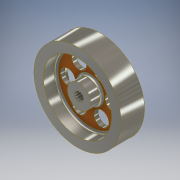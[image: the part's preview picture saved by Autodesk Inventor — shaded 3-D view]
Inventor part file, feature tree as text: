
AUTODESK INVENTOR PART (.ipt)
format: ipt  version: 2017 (Build 210142000, 142)  size: 212,480 bytes
history: native  units: mm
features: extrude x7, sketch x7, fillet x3, plane x2, chamfer x1
ambient origin geometry x8: Origin, YZ Plane, XZ Plane, XY Plane, X Axis, Y Axis, Z Axis, Center Point
bodies: Solid1 (feature_tree)
feature tree (20):
  extrude  "Extrusion1"  Depth=22.0mm TaperAngle=0.0deg
  extrude  "Extrusion2"  Depth=6.0mm TaperAngle=0.0deg
  extrude  "Extrusion3"  Depth=12.0mm TaperAngle=0.0deg
  plane  "Work Plane1"
  extrude  "Extrusion4"  Depth=22.0mm
  extrude  "Extrusion5"  Depth=22.0mm
  plane  "Work Plane2"
  extrude  "Extrusion6"  [1 undecoded]
  extrude  "Extrusion7"  Depth=10.0mm TaperAngle=0.0deg
  fillet  "Fillet1"  Radius=14.0mm
  fillet  "Fillet2"  Radius=60.0mm
  fillet  "Fillet3"  [1 undecoded]
  chamfer  "Chamfer1"  Distance=2.0mm
  sketch  "Sketch1"  dims[d0=82.0mm d1=22.0mm d2=0.0mm]
  sketch  "Sketch2"  dims[d3=64.0mm d4=6.0mm d5=0.0mm]
  sketch  "Sketch3"  dims[d6=64.0mm d7=12.0mm d8=0.0mm]
  sketch  "Sketch4"  dims[d9=1.5mm d10=22.0mm]
  sketch  "Sketch5"  dims[d11=22.0mm d12=0.0mm d13=8.0mm]
  sketch  "Sketch6"  dims[d14=22.0mm d15=0.0mm d16=-11.0mm]
  sketch  "Sketch7"  dims[d17=3.0mm d18=10.0mm d19=0.0mm d20=14.0mm d21=60.0mm d23=360.0deg d25=0.0mm d26=0.0mm d27=2.0mm d28=2.0mm d29=2.0mm d30=1.6mm d31=2.0mm d32=45.0deg d33=5.984419mm d34=20.97437mm]
note: 2 required parameter values undecoded (feature->parameter linkage not recoverable at this tier; creation-order binding heuristic only, values carry confidence <= 0.55)
